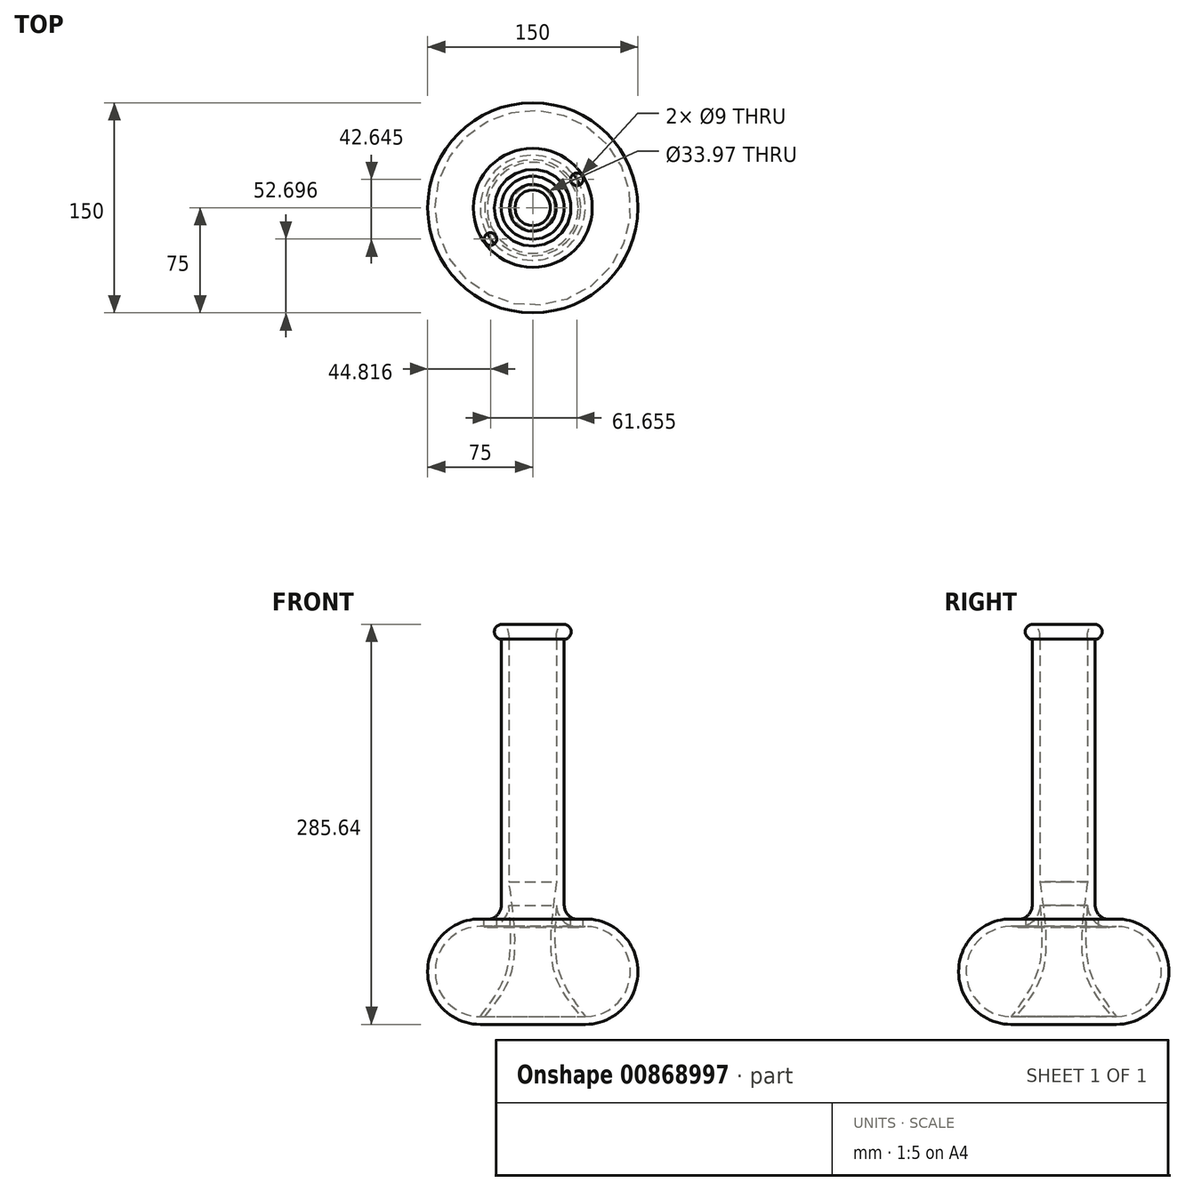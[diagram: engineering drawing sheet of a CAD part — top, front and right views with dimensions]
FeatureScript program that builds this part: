
annotation { "Feature Type Name" : "Feature", "Feature Type Description" : "" }
export const myFeature = defineFeature(function(context is Context, id is Id, definition is map)
    precondition{}
    {
        {
            var Q0;
            Q0=qCreatedBy(makeId("Front.planeOp"),FACE);
            var sketch = newSketch(context, id + "F0", { "sketchPlane" : qUnion([Q0])});
            skLineSegment(sketch, "E0", {"start": v(0, 0) * mm, "end": v(-37.5, 0) * mm});
            skLineSegment(sketch, "E1", {"start": v(-75, 37.5) * mm, "end": v(-75, 37.83) * mm});
            skPoint(sketch, "E2.visualSharp", {"position": v(-75, 0) * mm});
            skArc(sketch, "E2.filletArc", {"start": v(-75, 37.5) * mm, "mid": v(-64.02, 10.98) * mm, "end": v(-37.5, 0) * mm});
            skPoint(sketch, "E3.visualSharp", {"position": v(-75, 75) * mm});
            skArc(sketch, "E3.filletArc", {"start": v(-42.48, 75) * mm, "mid": v(-65.72, 62.52) * mm, "end": v(-75, 37.83) * mm});
            skLineSegment(sketch, "E4", {"start": v(-42.48, 75) * mm, "end": v(-32.48, 75) * mm});
            skLineSegment(sketch, "E5", {"start": v(-22.48, 275) * mm, "end": v(-22.48, 85) * mm});
            skPoint(sketch, "E6.visualSharp", {"position": v(-22.48, 75) * mm});
            skArc(sketch, "E6.filletArc", {"start": v(-32.48, 75) * mm, "mid": v(-25.41, 77.93) * mm, "end": v(-22.48, 85) * mm});
            skArc(sketch, "E7", {"start": v(-22.48, 285.62) * mm, "mid": v(-27.44, 280.3) * mm, "end": v(-22.48, 275) * mm});
            skLineSegment(sketch, "E8.0", {"start": v(0, 5.5) * mm, "end": v(-37.5, 5.5) * mm});
            skLineSegment(sketch, "E8.2", {"start": v(-16.98, 275) * mm, "end": v(-16.98, 85) * mm});
            skArc(sketch, "E8.3", {"start": v(-32.48, 69.5) * mm, "mid": v(-21.52, 74.04) * mm, "end": v(-16.98, 85) * mm});
            skLineSegment(sketch, "E8.4", {"start": v(-32.9, 69.5) * mm, "end": v(-32.48, 69.5) * mm});
            skFitSpline(sketch, "E9", {"points": [v(-16.98, 275) * mm, v(-22.48, 285.62) * mm], "startDerivative": vector(2.5, 17.63) * mm, "endDerivative": vector(-9.9, -1.31) * mm});
            skLineSegment(sketch, "E10", {"start": v(0, 0) * mm, "end": v(0, 5.5) * mm});
            skArc(sketch, "E11", {"start": v(-32.48, 69.5) * mm, "mid": v(-69.6, 40.21) * mm, "end": v(-37.5, 5.5) * mm});
            skFitSpline(sketch, "E12", {"points": [v(-37.5, 5.5) * mm, v(-18.32, 39.01) * mm, v(-16.98, 85) * mm], "startDerivative": vector(49.08, 65.79) * mm, "endDerivative": vector(-7.23, 92.82) * mm});
            skFitSpline(sketch, "E13", {"points": [v(-34.27, 5.5) * mm, v(-14.83, 38.7) * mm, v(-16.98, 101.9) * mm], "startDerivative": vector(54.92, 67.73) * mm, "endDerivative": vector(-17.37, 122.78) * mm});
            skSolve(sketch);
        }
        {
            var Q0;
            Q0 = qSketchRegion(id + "F0", true);
            var Q1;
            Q1=sQuery(id+"F0.wireOp",EDGE,"E10");
            revolve(context, id + "F1", {"surfaceOperationType" : NewSurfaceOperationType.NEW, "entities" : qUnion([Q0]), "axis" : qUnion([Q1]), "revolveType" : RevolveType.FULL});
        }
        {
            var Q0;
            Q0=qCreatedBy(makeId("Top.planeOp"),FACE);
            cPlane(context, id + "F2", {"entities" : qUnion([Q0]), "cplaneType" : CPlaneType.OFFSET, "offset" : 76.5 * mm, "width" : 150 * mm, "height" : 150 * mm});
        }
        {
            var Q0;
            Q0=qCreatedBy(id+"F2.planeOp",FACE);
            var sketch = newSketch(context, id + "F3", { "sketchPlane" : qUnion([Q0])});
            skCircle(sketch, "E14", {"center": v(-30.18, -22.3) * mm, "radius": 4.5 * mm});
            skCircle(sketch, "E15", {"center": v(31.47, 20.34) * mm, "radius": 4.5 * mm});
            skSolve(sketch);
        }
        {
            var Q0;
            Q0=makeQuery(id+"F3.imprint","IMPRINT",FACE,{"disambiguationData":[TD([[makeQuery(id+"F3.imprint","IMPRINT",EDGE,{"derivedFrom":sQuery(id+"F3.wireOp",EDGE,"E14")}),1.0]])]});
            extrude(context, id + "F4", {"entities" : qUnion([Q0]), "operationType" : NewBodyOperationType.REMOVE, "oppositeDirection" : true, "depth" : 15.1 * mm, "offsetDistance" : 25 * mm});
        }
        {
            var Q0;
            Q0 = qSketchRegion(id + "F3", true);
            extrude(context, id + "F5", {"entities" : qUnion([Q0]), "operationType" : NewBodyOperationType.REMOVE, "oppositeDirection" : true, "depth" : 25 * mm, "offsetDistance" : 25 * mm});
        }
        {
            var Q0;
            Q0=qCreatedBy(makeId("Right.planeOp"),FACE);
            cPlane(context, id + "F6", {"entities" : qUnion([Q0]), "cplaneType" : CPlaneType.OFFSET, "offset" : 31.2 * mm, "width" : 150 * mm, "height" : 150 * mm});
        }
    });
